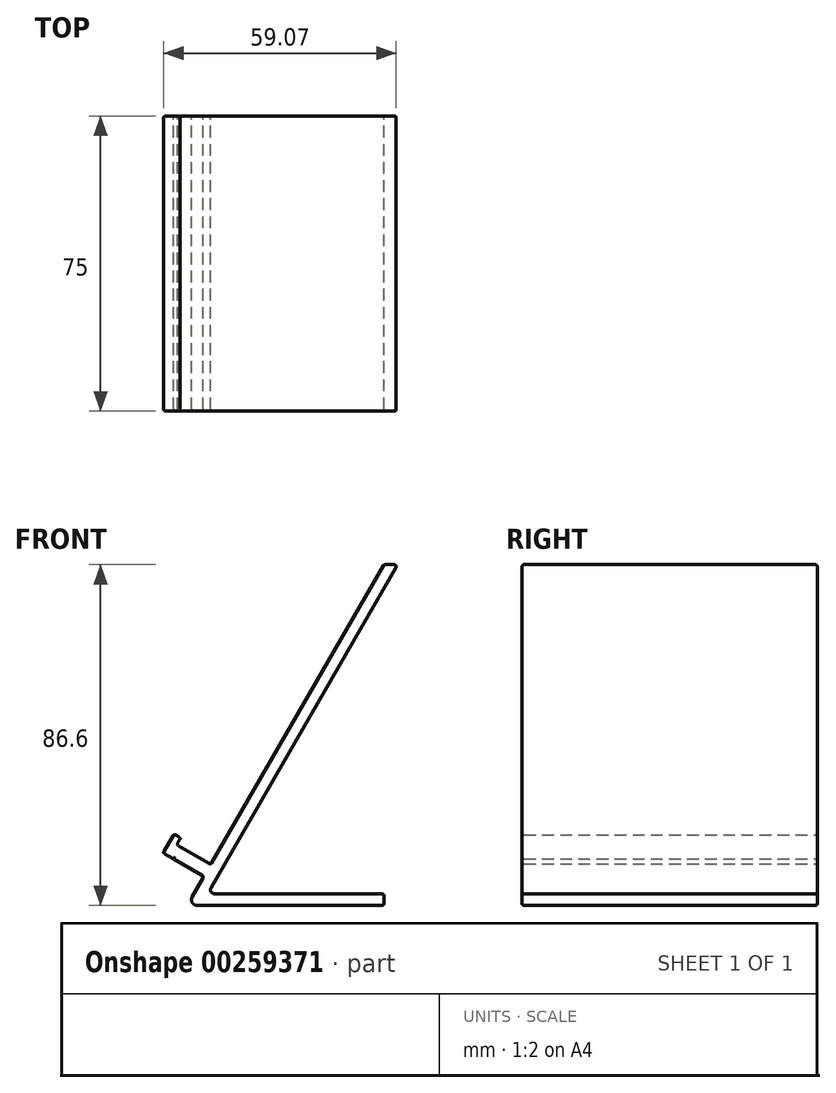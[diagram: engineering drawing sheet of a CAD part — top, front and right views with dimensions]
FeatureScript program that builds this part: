
annotation { "Feature Type Name" : "Feature", "Feature Type Description" : "" }
export const myFeature = defineFeature(function(context is Context, id is Id, definition is map)
    precondition{}
    {
        {
            var Q0;
            Q0=qCreatedBy(makeId("Front.planeOp"),FACE);
            var sketch = newSketch(context, id + "F0", { "sketchPlane" : qUnion([Q0])});
            skLineSegment(sketch, "E0", {"start": v(-0.5, 0) * mm, "end": v(-47.4, 0) * mm});
            skLineSegment(sketch, "E1", {"start": v(-48.7, 2.25) * mm, "end": v(-45.98, 6.97) * mm});
            skLineSegment(sketch, "E2", {"start": v(0, 86.6) * mm, "end": v(0, 0) * mm, "construction": true});
            skPoint(sketch, "E3.visualSharp", {"position": v(-50, 0) * mm});
            skArc(sketch, "E3.filletArc", {"start": v(-48.7, 2.25) * mm, "mid": v(-48.7, 0.75) * mm, "end": v(-47.4, 0) * mm});
            skLineSegment(sketch, "E4", {"start": v(-0.5, 3) * mm, "end": v(-43.07, 3) * mm});
            skLineSegment(sketch, "E5", {"start": v(-43.94, 4.5) * mm, "end": v(3.03, 85.85) * mm});
            skLineSegment(sketch, "E6", {"start": v(2.6, 86.6) * mm, "end": v(0.29, 86.6) * mm});
            skLineSegment(sketch, "E7", {"start": v(0, 2.5) * mm, "end": v(0, 0.5) * mm});
            skPoint(sketch, "E8.visualSharp", {"position": v(-44.8, 3) * mm});
            skArc(sketch, "E8.filletArc", {"start": v(-43.94, 4.5) * mm, "mid": v(-43.94, 3.5) * mm, "end": v(-43.07, 3) * mm});
            skPoint(sketch, "E9.visualSharp", {"position": v(0, 86.6) * mm});
            skArc(sketch, "E9.filletArc", {"start": v(0.29, 86.6) * mm, "mid": v(0.04, 86.54) * mm, "end": v(-0.14, 86.35) * mm});
            skPoint(sketch, "E10.visualSharp", {"position": v(3.46, 86.6) * mm});
            skArc(sketch, "E10.filletArc", {"start": v(3.03, 85.85) * mm, "mid": v(3.03, 86.35) * mm, "end": v(2.6, 86.6) * mm});
            skPoint(sketch, "E11.visualSharp", {"position": v(0, 3) * mm});
            skArc(sketch, "E11.filletArc", {"start": v(0, 2.5) * mm, "mid": v(-0.15, 2.85) * mm, "end": v(-0.5, 3) * mm});
            skPoint(sketch, "E12.visualSharp", {"position": v(0, 0) * mm});
            skArc(sketch, "E12.filletArc", {"start": v(-0.5, 0) * mm, "mid": v(-0.15, 0.15) * mm, "end": v(0, 0.5) * mm});
            skLineSegment(sketch, "E13", {"start": v(-46.16, 7.65) * mm, "end": v(-53.48, 11.88) * mm});
            skLineSegment(sketch, "E14", {"start": v(-52.21, 15.17) * mm, "end": v(-44.42, 10.67) * mm});
            skLineSegment(sketch, "E15", {"start": v(-52.4, 15.85) * mm, "end": v(-51.9, 16.72) * mm});
            skLineSegment(sketch, "E16", {"start": v(-52.08, 17.4) * mm, "end": v(-52.94, 17.9) * mm});
            skLineSegment(sketch, "E17", {"start": v(-53.63, 17.72) * mm, "end": v(-55.9, 13.78) * mm});
            skLineSegment(sketch, "E18", {"start": v(-55.7, 13.1) * mm, "end": v(-53.48, 11.88) * mm});
            skPoint(sketch, "E19.visualSharp", {"position": v(-56.16, 13.34) * mm});
            skArc(sketch, "E19.filletArc", {"start": v(-55.9, 13.78) * mm, "mid": v(-55.95, 13.4) * mm, "end": v(-55.7, 13.1) * mm});
            skPoint(sketch, "E20.visualSharp", {"position": v(-53.38, 18.15) * mm});
            skArc(sketch, "E20.filletArc", {"start": v(-52.94, 17.9) * mm, "mid": v(-53.32, 17.95) * mm, "end": v(-53.63, 17.72) * mm});
            skPoint(sketch, "E21.visualSharp", {"position": v(-51.64, 17.15) * mm});
            skArc(sketch, "E21.filletArc", {"start": v(-51.9, 16.72) * mm, "mid": v(-51.84, 17.1) * mm, "end": v(-52.08, 17.4) * mm});
            skPoint(sketch, "E22.visualSharp", {"position": v(-52.64, 15.42) * mm});
            skArc(sketch, "E22.filletArc", {"start": v(-52.4, 15.85) * mm, "mid": v(-52.44, 15.48) * mm, "end": v(-52.21, 15.17) * mm});
            skLineSegment(sketch, "E23.trimOffspring", {"start": v(-43.73, 10.85) * mm, "end": v(-0.14, 86.35) * mm});
            skPoint(sketch, "E24.visualSharp", {"position": v(-43.98, 10.42) * mm});
            skArc(sketch, "E24.filletArc", {"start": v(-44.42, 10.67) * mm, "mid": v(-44.04, 10.62) * mm, "end": v(-43.73, 10.85) * mm});
            skPoint(sketch, "E25.visualSharp", {"position": v(-45.73, 7.4) * mm});
            skArc(sketch, "E25.filletArc", {"start": v(-45.98, 6.97) * mm, "mid": v(-45.93, 7.34) * mm, "end": v(-46.16, 7.65) * mm});
            skSolve(sketch);
        }
        {
            var Q0;
            Q0=makeQuery(id+"F0.imprint","IMPRINT",FACE,{"disambiguationData":[TD([[makeQuery(id+"F0.imprint","IMPRINT",EDGE,{"derivedFrom":sQuery(id+"F0.wireOp",EDGE,"E0")}),-1.0]])]});
            extrude(context, id + "F1", {"entities" : qUnion([Q0]), "depth" : 75 * mm});
        }
        {
            var Q0;
            Q0=makeQuery(id+"F1.opExtrude","CAP_FACE",FACE,{"disambiguationData":[OSD([sQuery(id+"F0.wireOp",EDGE,"E0"),sQuery(id+"F0.wireOp",EDGE,"E1"),sQuery(id+"F0.wireOp",EDGE,"E3.filletArc"),sQuery(id+"F0.wireOp",EDGE,"E4"),sQuery(id+"F0.wireOp",EDGE,"E5"),sQuery(id+"F0.wireOp",EDGE,"E6"),sQuery(id+"F0.wireOp",EDGE,"E7"),sQuery(id+"F0.wireOp",EDGE,"E8.filletArc"),sQuery(id+"F0.wireOp",EDGE,"E9.filletArc"),sQuery(id+"F0.wireOp",EDGE,"E10.filletArc"),sQuery(id+"F0.wireOp",EDGE,"E11.filletArc"),sQuery(id+"F0.wireOp",EDGE,"E12.filletArc"),sQuery(id+"F0.wireOp",EDGE,"E13"),sQuery(id+"F0.wireOp",EDGE,"E14"),sQuery(id+"F0.wireOp",EDGE,"E15"),sQuery(id+"F0.wireOp",EDGE,"E16"),sQuery(id+"F0.wireOp",EDGE,"E17"),sQuery(id+"F0.wireOp",EDGE,"E18"),sQuery(id+"F0.wireOp",EDGE,"E19.filletArc"),sQuery(id+"F0.wireOp",EDGE,"E20.filletArc"),sQuery(id+"F0.wireOp",EDGE,"E21.filletArc"),sQuery(id+"F0.wireOp",EDGE,"E22.filletArc"),sQuery(id+"F0.wireOp",EDGE,"E23.trimOffspring"),sQuery(id+"F0.wireOp",EDGE,"E24.filletArc"),sQuery(id+"F0.wireOp",EDGE,"E25.filletArc")])],"isStart":false});
            var Q1;
            Q1=makeQuery(id+"F1.opExtrude","CAP_FACE",FACE,{"disambiguationData":[OSD([sQuery(id+"F0.wireOp",EDGE,"E0"),sQuery(id+"F0.wireOp",EDGE,"E1"),sQuery(id+"F0.wireOp",EDGE,"E3.filletArc"),sQuery(id+"F0.wireOp",EDGE,"E4"),sQuery(id+"F0.wireOp",EDGE,"E5"),sQuery(id+"F0.wireOp",EDGE,"E6"),sQuery(id+"F0.wireOp",EDGE,"E7"),sQuery(id+"F0.wireOp",EDGE,"E8.filletArc"),sQuery(id+"F0.wireOp",EDGE,"E9.filletArc"),sQuery(id+"F0.wireOp",EDGE,"E10.filletArc"),sQuery(id+"F0.wireOp",EDGE,"E11.filletArc"),sQuery(id+"F0.wireOp",EDGE,"E12.filletArc"),sQuery(id+"F0.wireOp",EDGE,"E13"),sQuery(id+"F0.wireOp",EDGE,"E14"),sQuery(id+"F0.wireOp",EDGE,"E15"),sQuery(id+"F0.wireOp",EDGE,"E16"),sQuery(id+"F0.wireOp",EDGE,"E17"),sQuery(id+"F0.wireOp",EDGE,"E18"),sQuery(id+"F0.wireOp",EDGE,"E19.filletArc"),sQuery(id+"F0.wireOp",EDGE,"E20.filletArc"),sQuery(id+"F0.wireOp",EDGE,"E21.filletArc"),sQuery(id+"F0.wireOp",EDGE,"E22.filletArc"),sQuery(id+"F0.wireOp",EDGE,"E23.trimOffspring"),sQuery(id+"F0.wireOp",EDGE,"E24.filletArc"),sQuery(id+"F0.wireOp",EDGE,"E25.filletArc")])],"isStart":true});
            fillet(context, id + "F2", {"entities" : qUnion([Q0, Q1]), "radius" : 0.5 * mm, "tangentPropagation" : true, "allowEdgeOverflow" : false});
        }
    });
